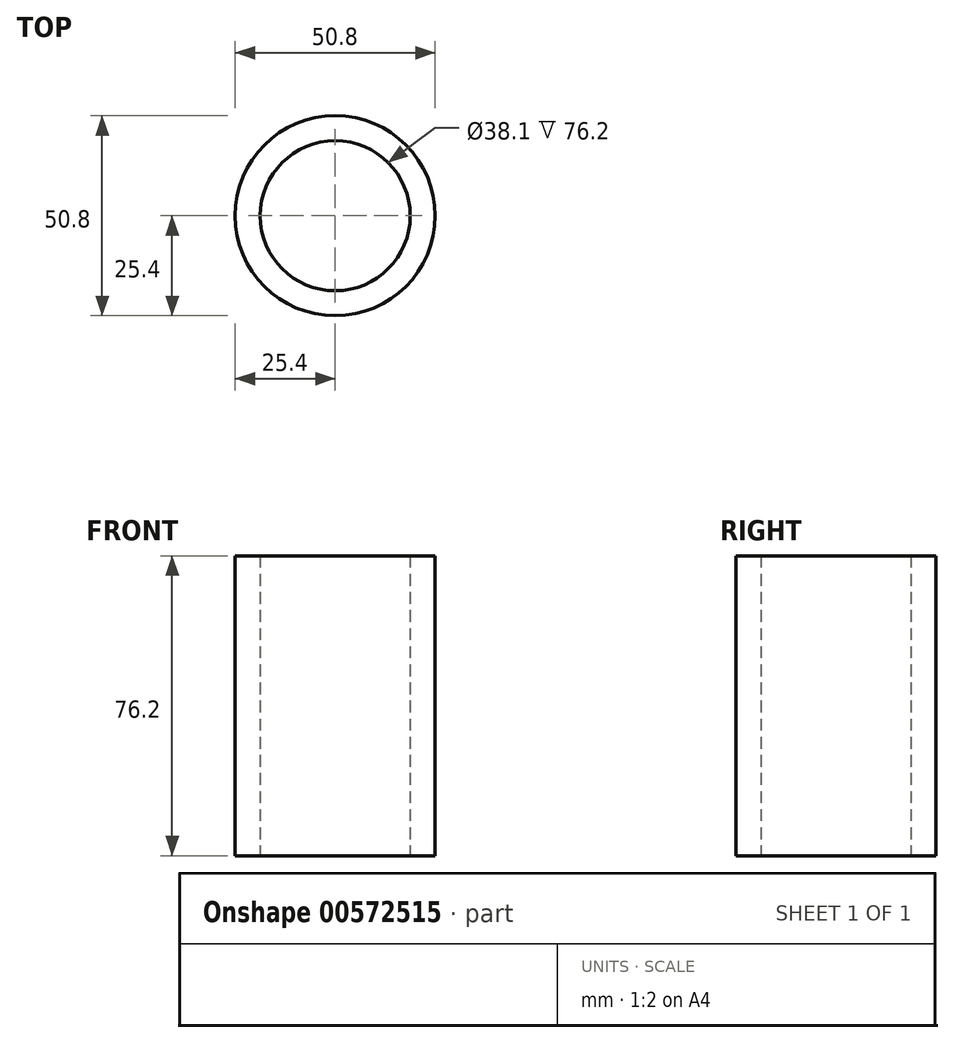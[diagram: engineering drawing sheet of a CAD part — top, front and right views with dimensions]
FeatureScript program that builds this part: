
annotation { "Feature Type Name" : "Feature", "Feature Type Description" : "" }
export const myFeature = defineFeature(function(context is Context, id is Id, definition is map)
    precondition{}
    {
        {
            var Q0;
            Q0=qCreatedBy(makeId("Top.planeOp"),FACE);
            var sketch = newSketch(context, id + "F0", { "sketchPlane" : qUnion([Q0])});
            skCircle(sketch, "E0", {"center": v(0, 0) * mm, "radius": 25.4 * mm});
            skCircle(sketch, "E1", {"center": v(0, 0) * mm, "radius": 19.05 * mm});
            skSolve(sketch);
        }
        {
            var Q0;
            Q0 = qSketchRegion(id + "F0", true);
            extrude(context, id + "F1", {"entities" : qUnion([Q0]), "depth" : 76.2 * mm, "offsetDistance" : 25.4 * mm});
        }
    });
